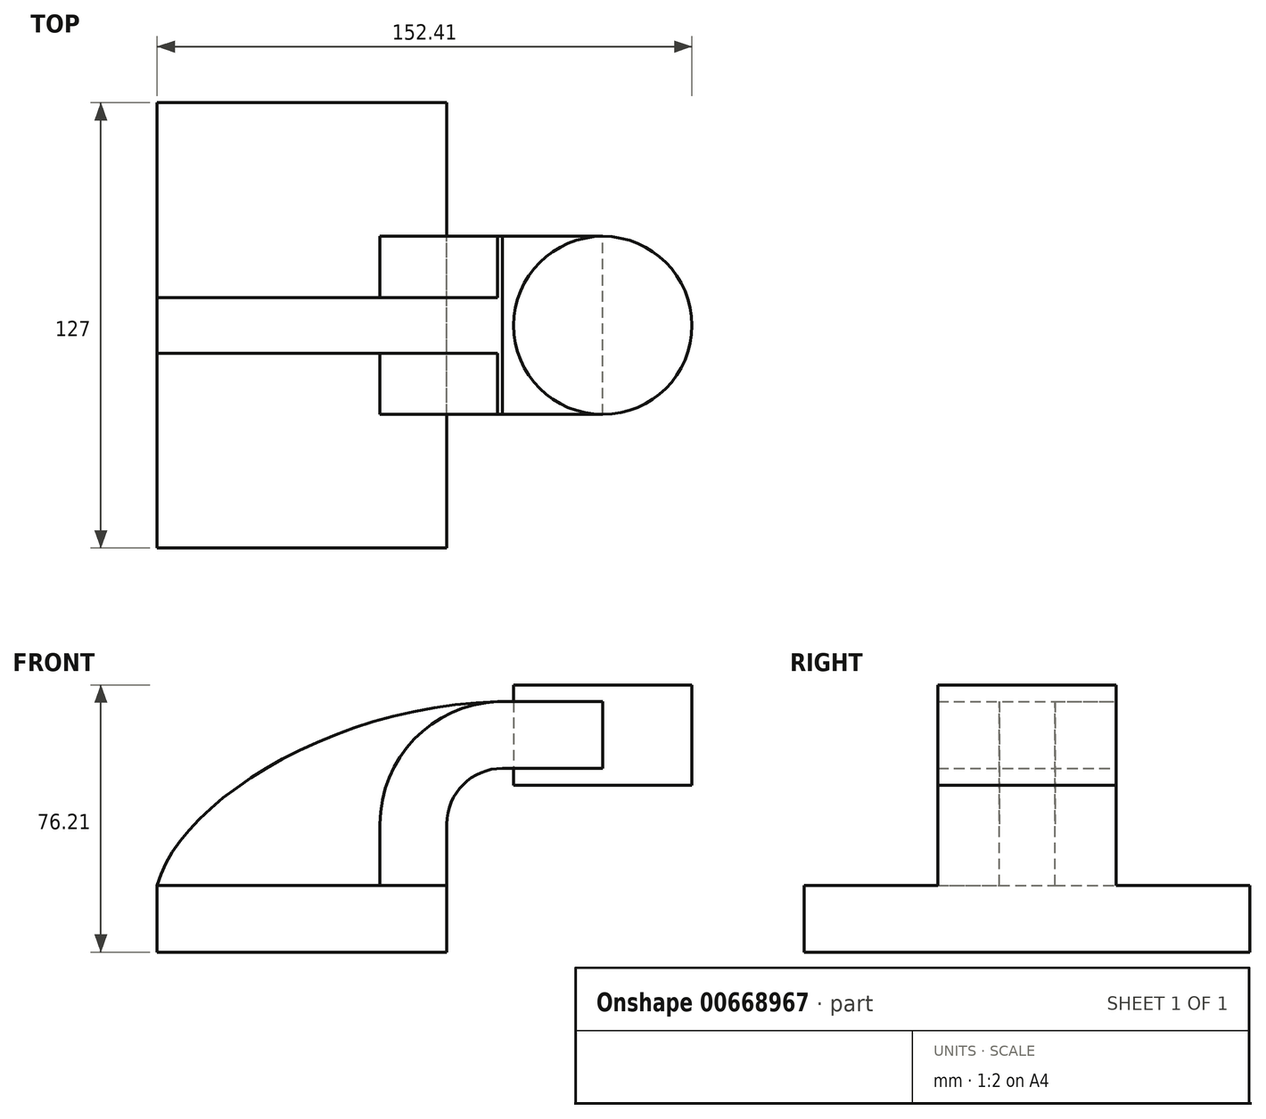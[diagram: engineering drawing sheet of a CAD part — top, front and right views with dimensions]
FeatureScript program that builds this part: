
annotation { "Feature Type Name" : "Feature", "Feature Type Description" : "" }
export const myFeature = defineFeature(function(context is Context, id is Id, definition is map)
    precondition{}
    {
        {
            var Q0;
            Q0=qCreatedBy(makeId("Front.planeOp"),FACE);
            var sketch = newSketch(context, id + "F0", { "sketchPlane" : qUnion([Q0])});
            skLineSegment(sketch, "E0.bottom", {"start": v(41.28, -9.52) * mm, "end": v(-41.28, -9.53) * mm});
            skLineSegment(sketch, "E0.top", {"start": v(41.27, 9.53) * mm, "end": v(-41.28, 9.53) * mm});
            skLineSegment(sketch, "E0.left", {"start": v(41.28, -9.52) * mm, "end": v(41.28, 9.53) * mm});
            skLineSegment(sketch, "E0.right", {"start": v(-41.28, -9.52) * mm, "end": v(-41.28, 9.53) * mm});
            skPoint(sketch, "E0.middle", {"position": v(0, 0) * mm});
            skLineSegment(sketch, "E1.bottom", {"start": v(111.12, 38.1) * mm, "end": v(60.32, 38.1) * mm});
            skLineSegment(sketch, "E1.top", {"start": v(111.12, 66.68) * mm, "end": v(60.32, 66.68) * mm});
            skLineSegment(sketch, "E1.left", {"start": v(111.12, 38.1) * mm, "end": v(111.12, 66.68) * mm});
            skLineSegment(sketch, "E1.right", {"start": v(60.32, 38.1) * mm, "end": v(60.32, 66.68) * mm});
            skPoint(sketch, "E1.middle", {"position": v(85.72, 52.39) * mm});
            skLineSegment(sketch, "E2", {"start": v(41.27, 9.53) * mm, "end": v(41.27, 27) * mm});
            skArc(sketch, "E3", {"start": v(41.27, 27) * mm, "mid": v(45.92, 38.23) * mm, "end": v(57.15, 42.88) * mm});
            skLineSegment(sketch, "E4", {"start": v(57.15, 42.88) * mm, "end": v(85.73, 42.88) * mm});
            skLineSegment(sketch, "E5.0", {"start": v(57.15, 61.93) * mm, "end": v(85.73, 61.93) * mm});
            skArc(sketch, "E5.1", {"start": v(22.23, 27) * mm, "mid": v(32.45, 51.7) * mm, "end": v(57.15, 61.93) * mm});
            skLineSegment(sketch, "E5.2", {"start": v(22.22, 9.53) * mm, "end": v(22.22, 27) * mm});
            skFitSpline(sketch, "E6", {"points": [v(-41.28, 9.53) * mm, v(57.15, 61.93) * mm], "startDerivative": vector(19.42, 72.3) * mm, "endDerivative": vector(141.93, 2.07) * mm});
            skLineSegment(sketch, "E7", {"start": v(85.73, 42.88) * mm, "end": v(85.73, 61.93) * mm});
            skLineSegment(sketch, "E8", {"start": v(85.73, 61.93) * mm, "end": v(85.72, 66.68) * mm});
            skLineSegment(sketch, "E9", {"start": v(85.72, 42.88) * mm, "end": v(85.72, 38.1) * mm});
            skSolve(sketch);
        }
        {
            var Q0;
            Q0=makeQuery(id+"F0.imprint","IMPRINT",FACE,{"disambiguationData":[TD([[makeQuery(id+"F0.imprint","IMPRINT",EDGE,{"derivedFrom":sQuery(id+"F0.wireOp",EDGE,"E0.bottom")}),-1.0]])]});
            extrude(context, id + "F1", {"entities" : qUnion([Q0]), "endBound" : BoundingType.SYMMETRIC, "depth" : 127 * mm, "offsetDistance" : 25.4 * mm});
        }
        {
            var Q0;
            {var subQ1=sQuery(id+"F0.wireOp",EDGE,"E2");Q0=makeQuery(id+"F0.imprint","IMPRINT",FACE,{"disambiguationData":[TD([[makeQuery(id+"F0.imprint","IMPRINT",EDGE,{"derivedFrom":subQ1}),1.0]])]});}
            var Q1;
            {var subQ0=sQuery(id+"F0.wireOp",EDGE,"E4");var subQ1=sQuery(id+"F0.wireOp",EDGE,"E1.right");var subQ2=makeQuery(id+"F0.imprint","INTERSECT",VERTEX,{"derivedFrom":[subQ1,subQ0]});Q1=makeQuery(id+"F0.imprint","IMPRINT",FACE,{"disambiguationData":[TD([[makeQuery(id+"F0.imprint","IMPRINT",EDGE,{"disambiguationData":[TD([[subQ2,-1.0]])],"derivedFrom":subQ1}),-1.0]])]});}
            extrude(context, id + "F2", {"entities" : qUnion([Q0, Q1]), "operationType" : NewBodyOperationType.ADD, "endBound" : BoundingType.SYMMETRIC, "depth" : 50.8 * mm, "offsetDistance" : 25.4 * mm});
        }
        {
            var Q0;
            {var subQ3=sQuery(id+"F0.wireOp",EDGE,"E5.2");Q0=makeQuery(id+"F0.imprint","IMPRINT",FACE,{"disambiguationData":[TD([[makeQuery(id+"F0.imprint","IMPRINT",EDGE,{"derivedFrom":subQ3}),1.0]])]});}
            extrude(context, id + "F3", {"entities" : qUnion([Q0]), "operationType" : NewBodyOperationType.ADD, "endBound" : BoundingType.SYMMETRIC, "depth" : 15.88 * mm, "offsetDistance" : 25.4 * mm});
        }
        {
            var Q0;
            {var subQ0=sQuery(id+"F0.wireOp",EDGE,"E1.left");Q0=makeQuery(id+"F0.imprint","IMPRINT",FACE,{"disambiguationData":[TD([[makeQuery(id+"F0.imprint","IMPRINT",EDGE,{"derivedFrom":subQ0}),1.0]])]});}
            var Q1;
            Q1=sQuery(id+"F0.wireOp",EDGE,"E7");
            revolve(context, id + "F4", {"entities" : qUnion([Q0]), "axis" : qUnion([Q1]), "revolveType" : RevolveType.FULL});
        }
    });
